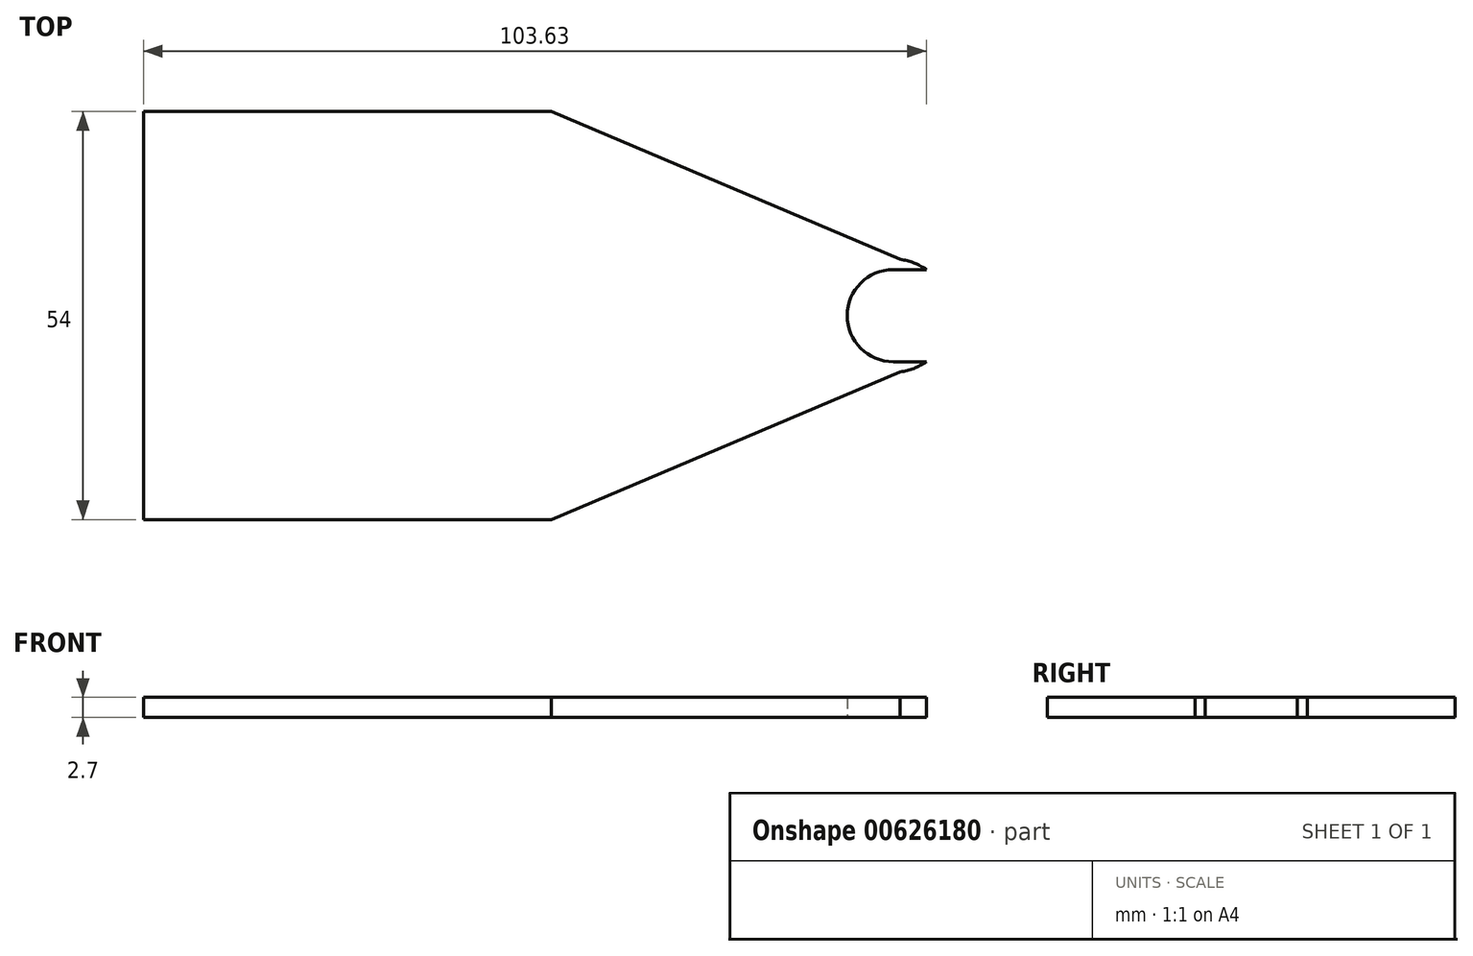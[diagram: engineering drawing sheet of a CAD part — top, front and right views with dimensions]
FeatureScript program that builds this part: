
annotation { "Feature Type Name" : "Feature", "Feature Type Description" : "" }
export const myFeature = defineFeature(function(context is Context, id is Id, definition is map)
    precondition{}
    {
        {
            var Q0;
            Q0=qCreatedBy(makeId("Top.planeOp"),FACE);
            var sketch = newSketch(context, id + "F0", { "sketchPlane" : qUnion([Q0])});
            skArc(sketch, "E0.3", {"start": v(12.81, -15.38) * mm, "mid": v(14.62, -14.93) * mm, "end": v(16.26, -14.04) * mm});
            skLineSegment(sketch, "E1", {"start": v(-33.37, 19.06) * mm, "end": v(12.81, -0.5) * mm});
            skLineSegment(sketch, "E2", {"start": v(-33.37, -34.94) * mm, "end": v(12.81, -15.38) * mm});
            skLineSegment(sketch, "E3", {"start": v(-33.37, 19.06) * mm, "end": v(-33.37, -34.94) * mm});
            skLineSegment(sketch, "E4.bottom", {"start": v(-33.37, 19.06) * mm, "end": v(-87.37, 19.06) * mm});
            skLineSegment(sketch, "E4.top", {"start": v(-33.37, -34.94) * mm, "end": v(-87.37, -34.94) * mm});
            skLineSegment(sketch, "E4.right", {"start": v(-87.37, 19.06) * mm, "end": v(-87.37, -34.94) * mm});
            skCircle(sketch, "E5", {"center": v(11.9, -7.94) * mm, "radius": 6.1 * mm});
            skLineSegment(sketch, "E6", {"start": v(11.9, -1.84) * mm, "end": v(16.26, -1.84) * mm});
            skLineSegment(sketch, "E7", {"start": v(11.9, -14.04) * mm, "end": v(16.26, -14.04) * mm});
            skArc(sketch, "E8.trimOffspring", {"start": v(16.26, -1.84) * mm, "mid": v(14.62, -0.95) * mm, "end": v(12.81, -0.5) * mm});
            skSolve(sketch);
        }
        {
            var Q0;
            {var subQ3=sQuery(id+"F0.wireOp",EDGE,"tGBmxwOM-yCkp-4iUj-8o48-6nUHxPGvIgvO");Q0=makeQuery(id+"F0.imprint","IMPRINT",FACE,{"disambiguationData":[TD([[makeQuery(id+"F0.imprint","IMPRINT",EDGE,{"derivedFrom":subQ3}),-1.0]])]});}
            var Q1;
            {var subQ6=sQuery(id+"F0.wireOp",EDGE,"ab868a46-4af4-4602-8ba4-63db27e046b7.1");Q1=makeQuery(id+"F0.imprint","IMPRINT",FACE,{"disambiguationData":[TD([[makeQuery(id+"F0.imprint","IMPRINT",EDGE,{"derivedFrom":subQ6}),-1.0]])]});}
            var Q2;
            Q2=makeQuery(id+"F0.imprint","IMPRINT",FACE,{"disambiguationData":[TD([[makeQuery(id+"F0.imprint","IMPRINT",EDGE,{"derivedFrom":sQuery(id+"F0.wireOp",EDGE,"ab868a46-4af4-4602-8ba4-63db27e046b7.1")}),1.0]])]});
            var Q3;
            {var subQ3=sQuery(id+"F0.wireOp",EDGE,"E4.bottom");Q3=makeQuery(id+"F0.imprint","IMPRINT",FACE,{"disambiguationData":[TD([[makeQuery(id+"F0.imprint","IMPRINT",EDGE,{"derivedFrom":subQ3}),1.0]])]});}
            var Q4;
            {var subQ3=sQuery(id+"F0.wireOp",EDGE,"vpylHigW-VZph-D9AM-dzcO-2BmP6p2nQhhF");Q4=makeQuery(id+"F0.imprint","IMPRINT",FACE,{"disambiguationData":[TD([[makeQuery(id+"F0.imprint","IMPRINT",EDGE,{"derivedFrom":subQ3}),1.0]])]});}
            var Q5;
            {var subQ0=sQuery(id+"F0.wireOp",EDGE,"E0.3");Q5=makeQuery(id+"F0.imprint","IMPRINT",FACE,{"disambiguationData":[TD([[makeQuery(id+"F0.imprint","IMPRINT",EDGE,{"derivedFrom":subQ0}),1.0]])]});}
            var Q6;
            {var subQ4=sQuery(id+"F0.wireOp",EDGE,"E6");Q6=makeQuery(id+"F0.imprint","IMPRINT",FACE,{"disambiguationData":[TD([[makeQuery(id+"F0.imprint","IMPRINT",EDGE,{"derivedFrom":subQ4}),1.0]])]});}
            extrude(context, id + "F1", {"entities" : qUnion([Q0, Q1, Q2, Q3, Q4, Q5, Q6]), "depth" : 2.7 * mm, "offsetDistance" : 25 * mm});
        }
    });
